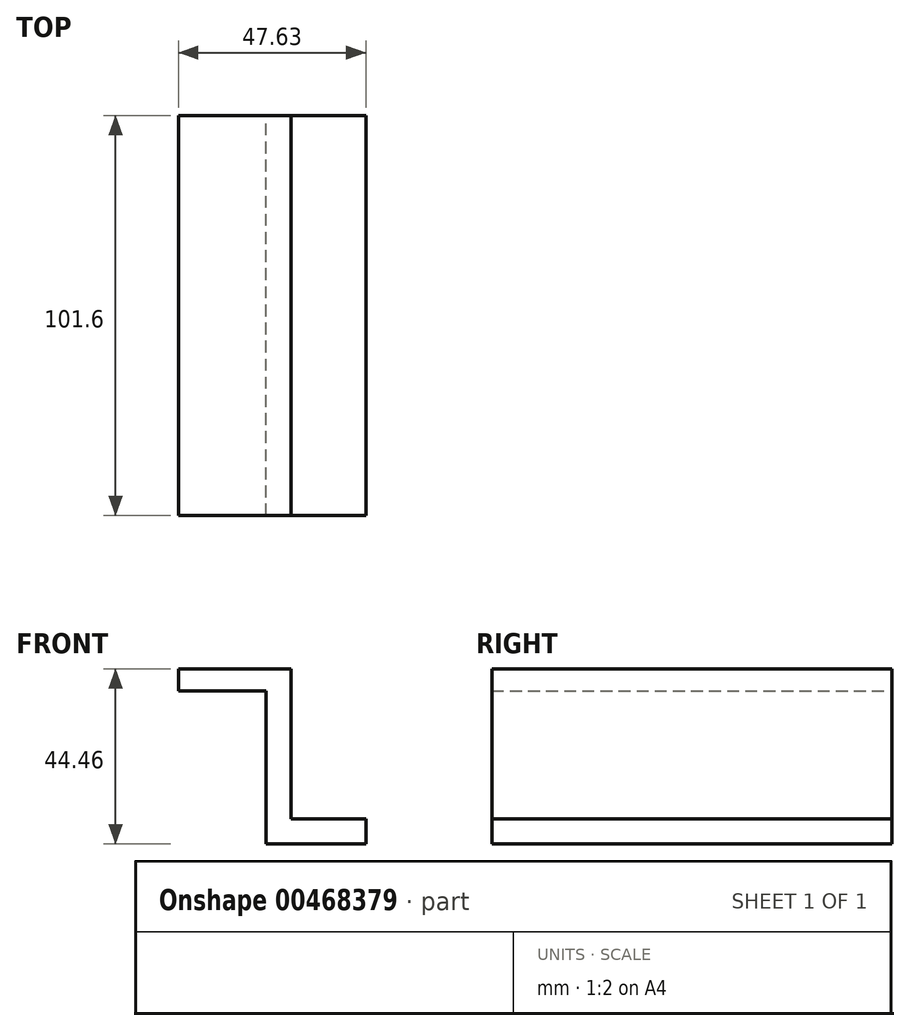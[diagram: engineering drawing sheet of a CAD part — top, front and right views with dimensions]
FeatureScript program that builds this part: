
annotation { "Feature Type Name" : "Feature", "Feature Type Description" : "" }
export const myFeature = defineFeature(function(context is Context, id is Id, definition is map)
    precondition{}
    {
        {
            var Q0;
            Q0=qCreatedBy(makeId("Front.planeOp"),FACE);
            var sketch = newSketch(context, id + "F0", { "sketchPlane" : qUnion([Q0])});
            skLineSegment(sketch, "E0.bottom", {"start": v(3.18, -22.23) * mm, "end": v(-3.17, -22.23) * mm});
            skLineSegment(sketch, "E0.top", {"start": v(3.17, 22.23) * mm, "end": v(-3.18, 22.23) * mm});
            skLineSegment(sketch, "E0.left", {"start": v(3.18, -15.88) * mm, "end": v(3.17, 22.23) * mm});
            skLineSegment(sketch, "E0.right", {"start": v(-3.17, -22.23) * mm, "end": v(-3.18, 16.64) * mm});
            skPoint(sketch, "E0.middle", {"position": v(0, 0) * mm});
            skLineSegment(sketch, "E1.bottom", {"start": v(-3.17, -22.23) * mm, "end": v(22.23, -22.23) * mm});
            skLineSegment(sketch, "E1.top", {"start": v(3.18, -15.88) * mm, "end": v(22.23, -15.88) * mm});
            skLineSegment(sketch, "E1.left", {"start": v(-3.17, -22.23) * mm, "end": v(-3.17, -15.88) * mm});
            skLineSegment(sketch, "E1.right", {"start": v(22.23, -22.23) * mm, "end": v(22.23, -15.88) * mm});
            skLineSegment(sketch, "E2.bottom", {"start": v(3.17, 22.23) * mm, "end": v(-25.4, 22.23) * mm});
            skLineSegment(sketch, "E2.top", {"start": v(-3.18, 16.64) * mm, "end": v(-25.4, 16.64) * mm});
            skLineSegment(sketch, "E2.left", {"start": v(3.17, 22.23) * mm, "end": v(3.17, 16.64) * mm});
            skLineSegment(sketch, "E2.right", {"start": v(-25.4, 22.22) * mm, "end": v(-25.4, 16.64) * mm});
            skSolve(sketch);
        }
        {
            var Q0;
            Q0 = qSketchRegion(id + "F0", true);
            extrude(context, id + "F1", {"entities" : qUnion([Q0]), "endBound" : BoundingType.SYMMETRIC, "depth" : 101.6 * mm});
        }
    });
